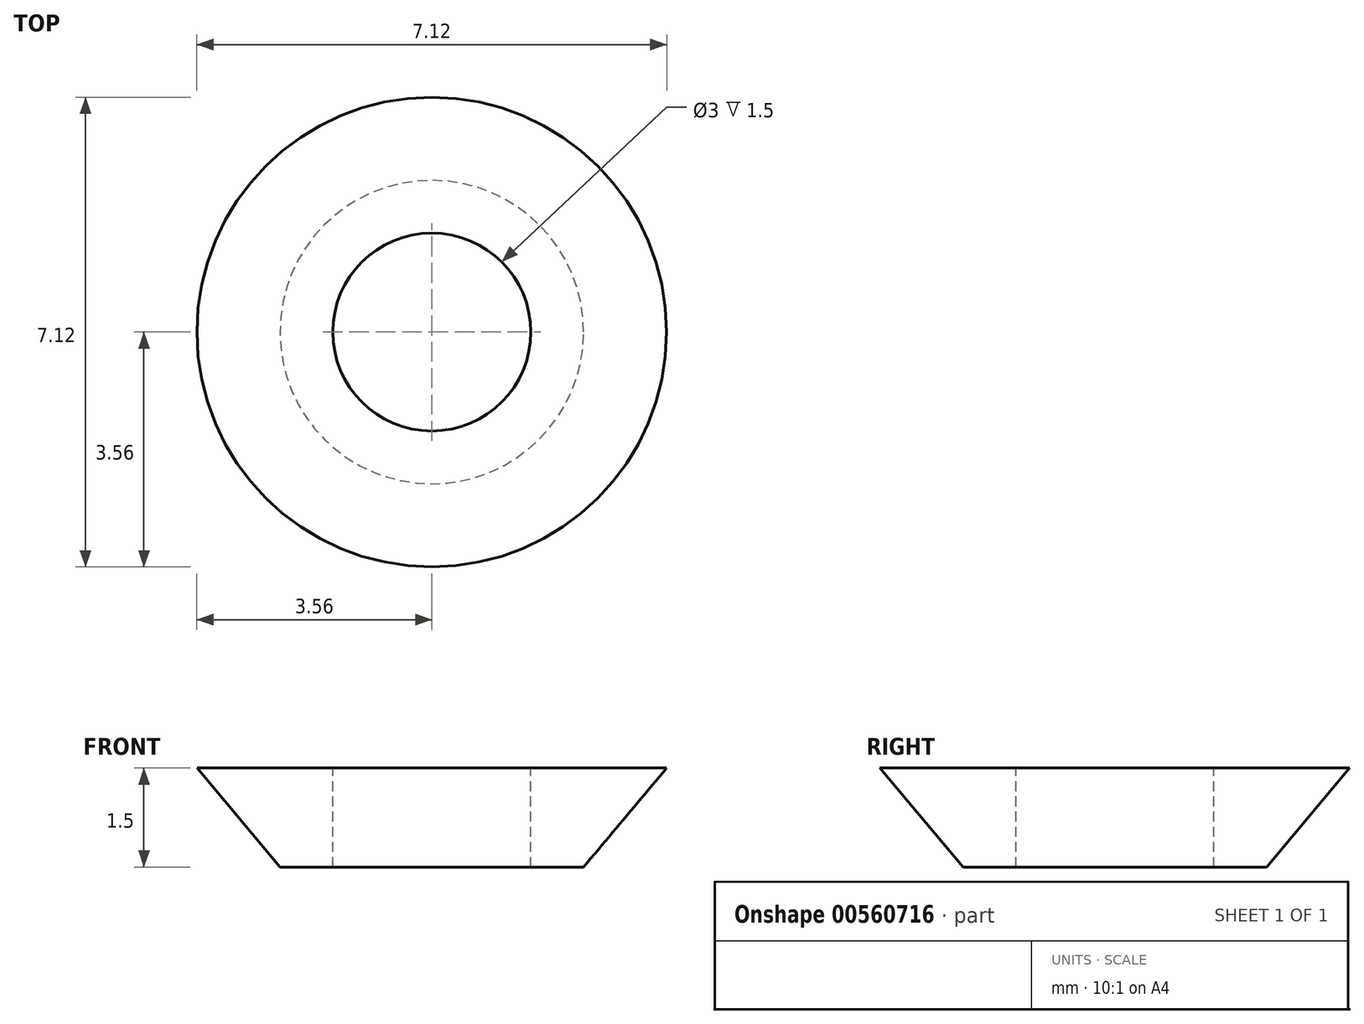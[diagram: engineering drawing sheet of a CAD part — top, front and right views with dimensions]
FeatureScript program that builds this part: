
annotation { "Feature Type Name" : "Feature", "Feature Type Description" : "" }
export const myFeature = defineFeature(function(context is Context, id is Id, definition is map)
    precondition{}
    {
        {
            var Q0;
            Q0=qCreatedBy(makeId("Top.planeOp"),FACE);
            var sketch = newSketch(context, id + "F0", { "sketchPlane" : qUnion([Q0])});
            skCircle(sketch, "E0", {"center": v(0, 0) * mm, "radius": 2.3 * mm});
            skSolve(sketch);
        }
        {
            var Q0;
            Q0 = qSketchRegion(id + "F0", true);
            extrude(context, id + "F1", {"entities" : qUnion([Q0]), "depth" : 1.5 * mm, "offsetDistance" : 25 * mm, "hasDraft" : true, "draftAngle" : 40 * degree});
        }
        {
            var Q0;
            Q0=makeQuery(id+"F1.opExtrude","CAP_FACE",FACE,{"disambiguationData":[OSD([sQuery(id+"F0.wireOp",EDGE,"E0")])],"isStart":false});
            var sketch = newSketch(context, id + "F2", { "sketchPlane" : qUnion([Q0])});
            skCircle(sketch, "E1", {"center": v(0, 0) * mm, "radius": 1.5 * mm});
            skSolve(sketch);
        }
        {
            var Q0;
            Q0=makeQuery(id+"F2.imprint","IMPRINT",FACE,{"disambiguationData":[TD([[makeQuery(id+"F2.imprint","IMPRINT",EDGE,{"derivedFrom":sQuery(id+"F2.wireOp",EDGE,"E1")}),1.0]])]});
            extrude(context, id + "F3", {"entities" : qUnion([Q0]), "operationType" : NewBodyOperationType.REMOVE, "oppositeDirection" : true, "depth" : 25 * mm, "offsetDistance" : 25 * mm});
        }
    });
